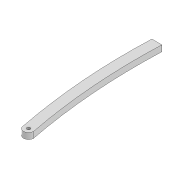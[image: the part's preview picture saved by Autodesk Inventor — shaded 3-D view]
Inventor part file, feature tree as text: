
AUTODESK INVENTOR PART (.ipt)
format: ipt  version: 2022 (Build 260153000, 153)  size: 106,496 bytes
history: native  units: mm
features: extrude x2, sketch x2
ambient origin geometry x8: Origin, YZ Plane, XZ Plane, XY Plane, X Axis, Y Axis, Z Axis, Center Point
bodies: Solid1 (feature_tree)
feature tree (4):
  extrude  "Extrusion1"  Depth=3.3mm
  extrude  "Extrusion2"  Depth=10.0mm
  sketch  "Sketch1"  dims[d0=3.3mm d1=3.3mm]
  sketch  "Sketch2"  dims[d2=10.0mm d3=288.984mm d6=6.0mm d7=0.0mm d14=3.3mm d15=231.585mm d18=600.0mm d19=600.0mm d20=10.0mm d21=0.0mm]
